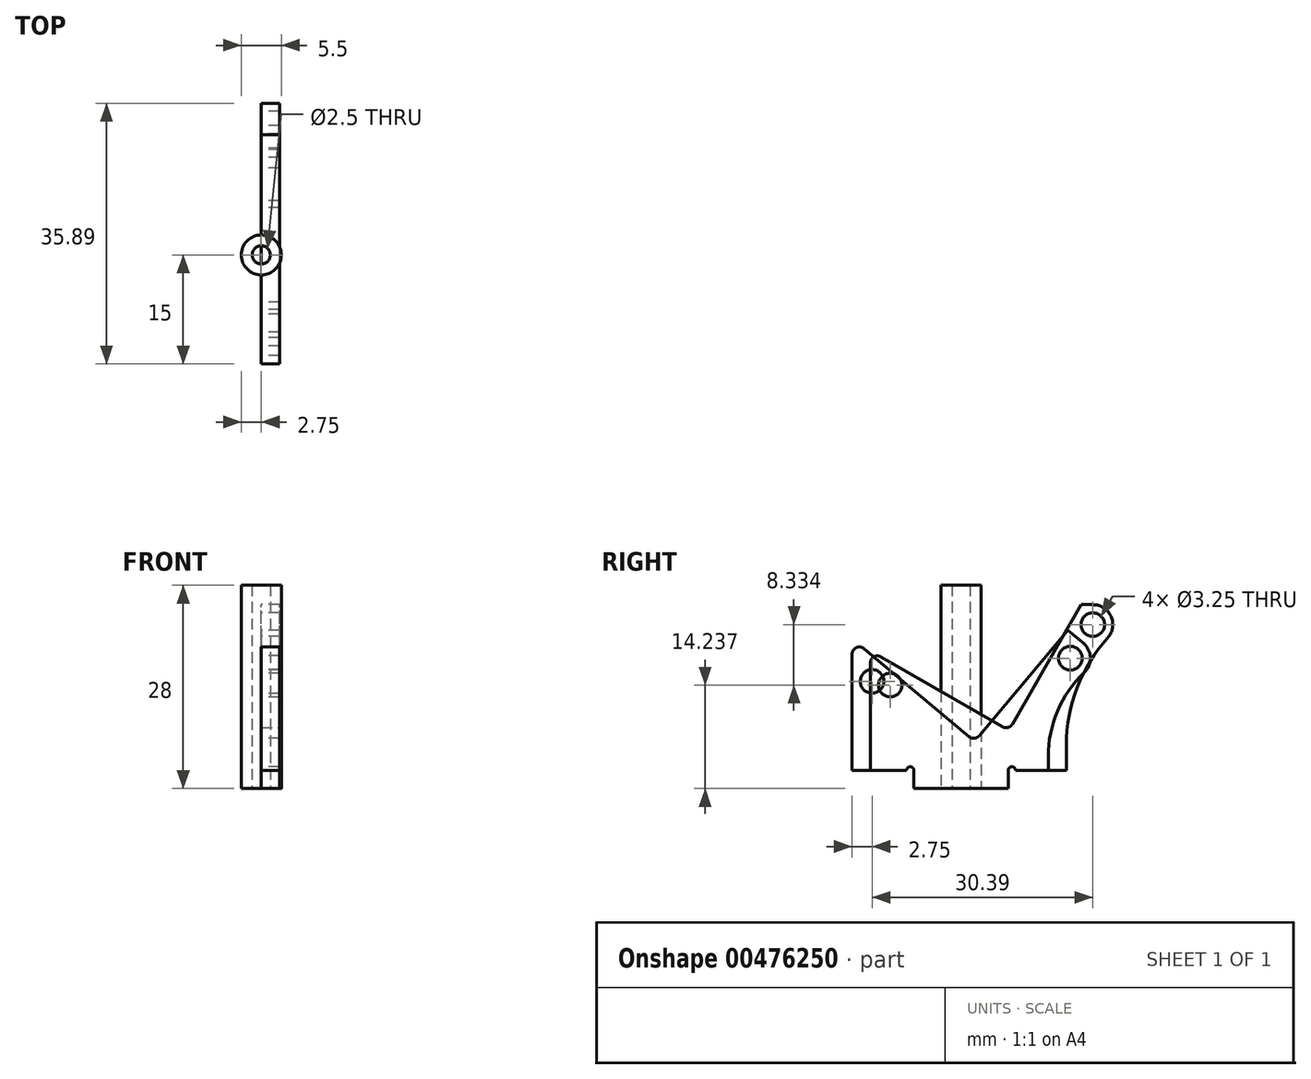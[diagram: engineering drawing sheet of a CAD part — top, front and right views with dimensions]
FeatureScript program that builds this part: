
annotation { "Feature Type Name" : "Feature", "Feature Type Description" : "" }
export const myFeature = defineFeature(function(context is Context, id is Id, definition is map)
    precondition{}
    {
        {
            var Q0;
            Q0=qCreatedBy(makeId("Right.planeOp"),FACE);
            var sketch = newSketch(context, id + "F0", { "sketchPlane" : qUnion([Q0])});
            skLineSegment(sketch, "E0", {"start": v(-12.5, 2.5) * mm, "end": v(-12.5, 17.27) * mm});
            skLineSegment(sketch, "E1", {"start": v(-11, 18.13) * mm, "end": v(6.55, 8) * mm});
            skCircle(sketch, "E2", {"center": v(-9.75, 14.24) * mm, "radius": 2.75 * mm, "construction": true});
            skLineSegment(sketch, "E3", {"start": v(6.55, 8) * mm, "end": v(16.55, 25.32) * mm});
            skLineSegment(sketch, "E4", {"start": v(16.55, 25.32) * mm, "end": v(18.14, 25.32) * mm});
            skLineSegment(sketch, "E5", {"start": v(14.5, 2.5) * mm, "end": v(7.5, 2.5) * mm});
            skPoint(sketch, "E6.orphan", {"position": v(-12.5, 0) * mm});
            skLineSegment(sketch, "E7", {"start": v(-6.5, 2.5) * mm, "end": v(-6.5, 0) * mm});
            skLineSegment(sketch, "E8", {"start": v(6.5, 2.5) * mm, "end": v(6.5, 0) * mm});
            skLineSegment(sketch, "E9", {"start": v(6.5, 0) * mm, "end": v(-6.5, 0) * mm});
            skArc(sketch, "E10", {"start": v(-6.5, 2.5) * mm, "mid": v(-7, 3) * mm, "end": v(-7.5, 2.5) * mm});
            skLineSegment(sketch, "E11.trimOffspring", {"start": v(-7.5, 2.5) * mm, "end": v(-12.5, 2.5) * mm});
            skArc(sketch, "E12.MirrorCS", {"start": v(6.5, 2.5) * mm, "mid": v(7, 3) * mm, "end": v(7.5, 2.5) * mm});
            skPoint(sketch, "E13.visualSharp", {"position": v(-12.5, 19) * mm});
            skArc(sketch, "E13.filletArc", {"start": v(-11, 18.13) * mm, "mid": v(-12, 18.13) * mm, "end": v(-12.5, 17.27) * mm});
            skCircle(sketch, "E14", {"center": v(-9.75, 14.24) * mm, "radius": 1.63 * mm});
            skCircle(sketch, "E15", {"center": v(18.14, 22.57) * mm, "radius": 1.63 * mm});
            skLineSegment(sketch, "E16", {"start": v(14.5, 5.97) * mm, "end": v(14.5, 2.5) * mm});
            skArc(sketch, "E17.trimOffspring", {"start": v(20.18, 20.73) * mm, "mid": v(20.65, 23.69) * mm, "end": v(18.14, 25.32) * mm});
            skArc(sketch, "E18.filletArc", {"start": v(20.18, 20.73) * mm, "mid": v(15.97, 13.88) * mm, "end": v(14.5, 5.97) * mm});
            skSolve(sketch);
        }
        {
            var Q0;
            Q0=makeQuery(id+"F0.imprint","IMPRINT",FACE,{"disambiguationData":[TD([[makeQuery(id+"F0.imprint","IMPRINT",EDGE,{"derivedFrom":sQuery(id+"F0.wireOp",EDGE,"E0")}),-1.0]])]});
            extrude(context, id + "F1", {"entities" : qUnion([Q0]), "depth" : 2.5 * mm, "offsetDistance" : 25 * mm});
        }
        {
            var Q0;
            Q0=makeQuery(id+"F1.opExtrude","SWEPT_EDGE",EDGE,{"disambiguationData":[OSD([sQuery(id+"F0.wireOp",EDGE,"E1"),sQuery(id+"F0.wireOp",EDGE,"E3")])]});
            fillet(context, id + "F2", {"entities" : qUnion([Q0]), "radius" : 1 * mm, "tangentPropagation" : true, "allowEdgeOverflow" : false});
        }
        {
            var Q0;
            Q0=qCreatedBy(makeId("Right.planeOp"),FACE);
            var sketch = newSketch(context, id + "F3", { "sketchPlane" : qUnion([Q0])});
            skLineSegment(sketch, "E19.bottom", {"start": v(-6.5, 2.5) * mm, "end": v(6.5, 2.5) * mm, "construction": true});
            skLineSegment(sketch, "E19.top", {"start": v(-6.5, 0) * mm, "end": v(6.5, 0) * mm});
            skLineSegment(sketch, "E19.left", {"start": v(-6.5, 2.5) * mm, "end": v(-6.5, 0) * mm});
            skLineSegment(sketch, "E19.right", {"start": v(6.5, 2.5) * mm, "end": v(6.5, 0) * mm});
            skLineSegment(sketch, "E20", {"start": v(-15, 2.5) * mm, "end": v(-15, 18.5) * mm});
            skLineSegment(sketch, "E21", {"start": v(-13.36, 19.26) * mm, "end": v(1.09, 7.14) * mm});
            skLineSegment(sketch, "E22", {"start": v(2.5, 7.27) * mm, "end": v(14.7, 21.82) * mm});
            skCircle(sketch, "E23", {"center": v(-12.25, 14.74) * mm, "radius": 2.75 * mm, "construction": true});
            skCircle(sketch, "E24", {"center": v(-12.25, 14.74) * mm, "radius": 1.63 * mm});
            skArc(sketch, "E25", {"start": v(16.95, 15.96) * mm, "mid": v(17.8, 18.04) * mm, "end": v(16.82, 20.05) * mm});
            skLineSegment(sketch, "E26", {"start": v(14.7, 21.82) * mm, "end": v(16.82, 20.05) * mm});
            skLineSegment(sketch, "E27", {"start": v(7.5, 2.5) * mm, "end": v(12, 2.5) * mm});
            skLineSegment(sketch, "E28", {"start": v(12, 2.5) * mm, "end": v(12, 4.39) * mm});
            skArc(sketch, "E29.filletArc", {"start": v(16.95, 15.96) * mm, "mid": v(13.29, 10.68) * mm, "end": v(12, 4.39) * mm});
            skCircle(sketch, "E30", {"center": v(15.05, 17.95) * mm, "radius": 1.63 * mm});
            skPoint(sketch, "E31.visualSharp", {"position": v(-15, 20.64) * mm});
            skArc(sketch, "E31.filletArc", {"start": v(-13.36, 19.26) * mm, "mid": v(-14.42, 19.4) * mm, "end": v(-15, 18.5) * mm});
            skPoint(sketch, "E32.visualSharp", {"position": v(1.85, 6.5) * mm});
            skArc(sketch, "E32.filletArc", {"start": v(1.09, 7.14) * mm, "mid": v(1.82, 6.91) * mm, "end": v(2.5, 7.27) * mm});
            skArc(sketch, "E33", {"start": v(-6.5, 2.5) * mm, "mid": v(-7, 3) * mm, "end": v(-7.5, 2.5) * mm});
            skLineSegment(sketch, "E34.trimOffspring", {"start": v(-7.5, 2.5) * mm, "end": v(-15, 2.5) * mm});
            skArc(sketch, "E35.MirrorCS", {"start": v(6.5, 2.5) * mm, "mid": v(7, 3) * mm, "end": v(7.5, 2.5) * mm});
            skSolve(sketch);
        }
        {
            var Q0;
            Q0=makeQuery(id+"F3.imprint","IMPRINT",FACE,{"disambiguationData":[TD([[makeQuery(id+"F3.imprint","IMPRINT",EDGE,{"derivedFrom":sQuery(id+"F3.wireOp",EDGE,"E19.top")}),1.0]])]});
            extrude(context, id + "F4", {"entities" : qUnion([Q0]), "depth" : 2.5 * mm, "offsetDistance" : 25 * mm});
        }
        {
            var Q0;
            Q0=qCreatedBy(makeId("Top.planeOp"),FACE);
            var sketch = newSketch(context, id + "F5", { "sketchPlane" : qUnion([Q0])});
            skCircle(sketch, "E36", {"center": v(0, 0) * mm, "radius": 2.75 * mm});
            skCircle(sketch, "E37", {"center": v(0, 0) * mm, "radius": 1.25 * mm});
            skSolve(sketch);
        }
        {
            var Q0;
            Q0=makeQuery(id+"F5.imprint","IMPRINT",FACE,{"disambiguationData":[TD([[makeQuery(id+"F5.imprint","IMPRINT",EDGE,{"derivedFrom":sQuery(id+"F5.wireOp",EDGE,"E36")}),1.0]])]});
            extrude(context, id + "F6", {"entities" : qUnion([Q0]), "depth" : 28 * mm, "offsetDistance" : 25 * mm});
        }
    });
